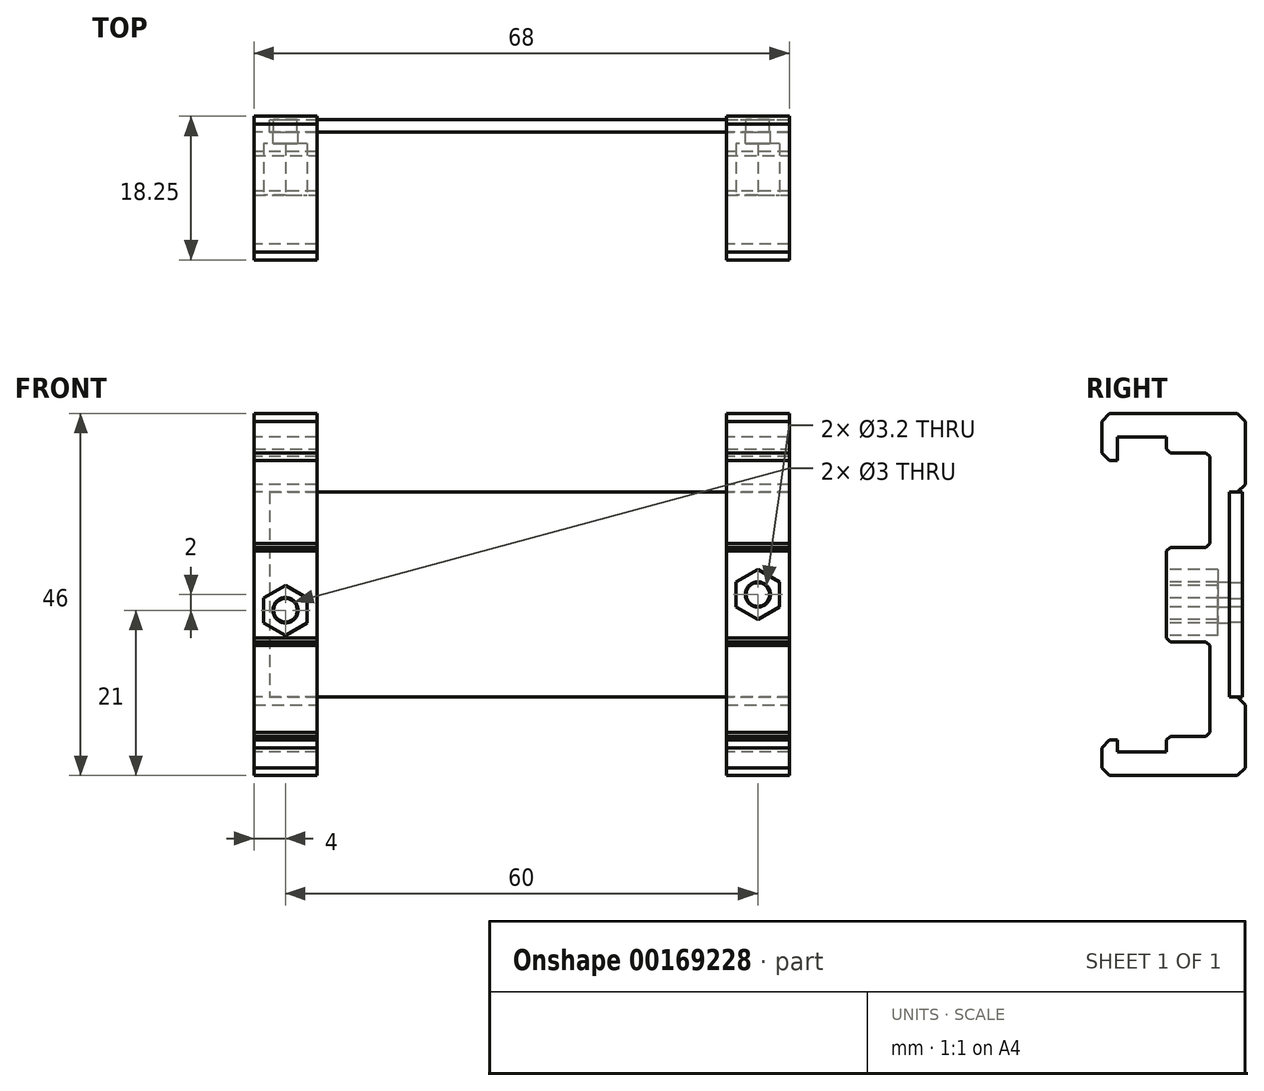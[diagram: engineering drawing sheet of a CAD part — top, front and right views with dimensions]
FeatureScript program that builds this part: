
annotation { "Feature Type Name" : "Feature", "Feature Type Description" : "" }
export const myFeature = defineFeature(function(context is Context, id is Id, definition is map)
    precondition{}
    {
        {
            var Q0;
            Q0=qCreatedBy(makeId("Front.planeOp"),FACE);
            var sketch = newSketch(context, id + "F0", { "sketchPlane" : qUnion([Q0])});
            skLineSegment(sketch, "E0.bottom", {"start": v(-33, 13) * mm, "end": v(33, 13) * mm});
            skLineSegment(sketch, "E0.top", {"start": v(-33, -13) * mm, "end": v(33, -13) * mm});
            skLineSegment(sketch, "E0.left", {"start": v(-33, 13) * mm, "end": v(-33, -13) * mm});
            skLineSegment(sketch, "E0.right", {"start": v(33, 13) * mm, "end": v(33, -13) * mm});
            skPoint(sketch, "E0.middle", {"position": v(0, 0) * mm});
            skCircle(sketch, "E1", {"center": v(-31, -2) * mm, "radius": 1.5 * mm});
            skCircle(sketch, "E2", {"center": v(29, 0) * mm, "radius": 1.5 * mm});
            skLineSegment(sketch, "E3", {"start": v(29, 0) * mm, "end": v(-31, 0) * mm, "construction": true});
            skSolve(sketch);
        }
        {
            var Q0;
            Q0=makeQuery(id+"F0.imprint","IMPRINT",FACE,{"disambiguationData":[TD([[makeQuery(id+"F0.imprint","IMPRINT",EDGE,{"derivedFrom":sQuery(id+"F0.wireOp",EDGE,"E0.bottom")}),-1.0]])]});
            extrude(context, id + "F1", {"entities" : qUnion([Q0]), "depth" : 1.6 * mm, "offsetDistance" : 25 * mm, "symmetric" : true});
        }
        {
            var Q0;
            Q0=sQuery(id+"F0.wireOp",VERTEX,"E2.center");
            var Q1;
            Q1=makeQuery(id+"F1.opExtrude","CAP_EDGE",EDGE,{"disambiguationData":[OSD([sQuery(id+"F0.wireOp",EDGE,"E0.bottom")])],"isStart":true});
            cPlane(context, id + "F2", {"entities" : qUnion([Q0, Q1]), "cplaneType" : CPlaneType.LINE_POINT, "offset" : 25 * mm, "width" : 150 * mm, "height" : 150 * mm});
        }
        {
            var Q0;
            Q0=qCreatedBy(id+"F2.planeOp",FACE);
            var sketch = newSketch(context, id + "F3", { "sketchPlane" : qUnion([Q0])});
            skLineSegment(sketch, "E4", {"start": v(-17.05, 17) * mm, "end": v(-17.05, 23) * mm});
            skLineSegment(sketch, "E5", {"start": v(-17.05, 23) * mm, "end": v(1.2, 23) * mm});
            skLineSegment(sketch, "E6", {"start": v(1.2, 23) * mm, "end": v(1.2, -23) * mm});
            skLineSegment(sketch, "E7", {"start": v(1.2, -23) * mm, "end": v(-17.05, -23) * mm});
            skLineSegment(sketch, "E8", {"start": v(-17.05, -23) * mm, "end": v(-17.05, -18.5) * mm});
            skLineSegment(sketch, "E9", {"start": v(-17.05, -18.5) * mm, "end": v(-15.05, -18.5) * mm});
            skLineSegment(sketch, "E10", {"start": v(-15.05, -18.5) * mm, "end": v(-15.05, -20) * mm});
            skLineSegment(sketch, "E11", {"start": v(-15.05, -20) * mm, "end": v(-8.8, -20) * mm});
            skLineSegment(sketch, "E12", {"start": v(-8.8, -20) * mm, "end": v(-8.8, 20) * mm});
            skLineSegment(sketch, "E13", {"start": v(-8.8, 20) * mm, "end": v(-15.05, 20) * mm});
            skLineSegment(sketch, "E14", {"start": v(-15.05, 20) * mm, "end": v(-15.05, 17) * mm});
            skLineSegment(sketch, "E15", {"start": v(-15.05, 17) * mm, "end": v(-17.05, 17) * mm});
            skPoint(sketch, "E16", {"position": v(1.2, 0) * mm});
            skLineSegment(sketch, "E17.0", {"start": v(-0.8, 13) * mm, "end": v(-0.8, -13) * mm});
            skLineSegment(sketch, "E18", {"start": v(-0.8, 13) * mm, "end": v(1.2, 13) * mm});
            skLineSegment(sketch, "E19", {"start": v(-0.8, -13) * mm, "end": v(1.2, -13) * mm});
            skLineSegment(sketch, "E20", {"start": v(-8.8, 18) * mm, "end": v(-3.3, 18) * mm});
            skLineSegment(sketch, "E21", {"start": v(-3.3, 18) * mm, "end": v(-3.3, 6) * mm});
            skLineSegment(sketch, "E22", {"start": v(-3.3, 6) * mm, "end": v(-8.8, 6) * mm});
            skLineSegment(sketch, "E23.MirrorCS", {"start": v(-8.8, -18) * mm, "end": v(-3.3, -18) * mm});
            skLineSegment(sketch, "E24.MirrorCS", {"start": v(-3.3, -18) * mm, "end": v(-3.3, -6) * mm});
            skLineSegment(sketch, "E25.MirrorCS", {"start": v(-3.3, -6) * mm, "end": v(-8.8, -6) * mm});
            skSolve(sketch);
        }
        {
            var Q0;
            Q0=makeQuery(id+"F3.imprint","IMPRINT",FACE,{"disambiguationData":[TD([[makeQuery(id+"F3.imprint","IMPRINT",EDGE,{"derivedFrom":sQuery(id+"F3.wireOp",EDGE,"E4")}),-1.0]])]});
            extrude(context, id + "F4", {"entities" : qUnion([Q0]), "depth" : 8 * mm, "offsetDistance" : 25 * mm, "symmetric" : true});
        }
        {
            var Q0;
            Q0=makeQuery(id+"F4.opExtrude","SWEPT_EDGE",EDGE,{"disambiguationData":[OSD([sQuery(id+"F3.wireOp",EDGE,"E12"),sQuery(id+"F3.wireOp",EDGE,"E20")])]});
            var Q1;
            Q1=makeQuery(id+"F4.opExtrude","SWEPT_EDGE",EDGE,{"disambiguationData":[OSD([sQuery(id+"F3.wireOp",EDGE,"E20"),sQuery(id+"F3.wireOp",EDGE,"E21")])]});
            var Q2;
            Q2=makeQuery(id+"F4.opExtrude","SWEPT_EDGE",EDGE,{"disambiguationData":[OSD([sQuery(id+"F3.wireOp",EDGE,"E21"),sQuery(id+"F3.wireOp",EDGE,"E22")])]});
            var Q3;
            Q3=makeQuery(id+"F4.opExtrude","SWEPT_EDGE",EDGE,{"disambiguationData":[OSD([sQuery(id+"F3.wireOp",EDGE,"E12"),sQuery(id+"F3.wireOp",EDGE,"E22")])]});
            var Q4;
            Q4=makeQuery(id+"F4.opExtrude","SWEPT_EDGE",EDGE,{"disambiguationData":[OSD([sQuery(id+"F3.wireOp",EDGE,"E12"),sQuery(id+"F3.wireOp",EDGE,"E25.MirrorCS")])]});
            var Q5;
            Q5=makeQuery(id+"F4.opExtrude","SWEPT_EDGE",EDGE,{"disambiguationData":[OSD([sQuery(id+"F3.wireOp",EDGE,"E24.MirrorCS"),sQuery(id+"F3.wireOp",EDGE,"E25.MirrorCS")])]});
            var Q6;
            Q6=makeQuery(id+"F4.opExtrude","SWEPT_EDGE",EDGE,{"disambiguationData":[OSD([sQuery(id+"F3.wireOp",EDGE,"E23.MirrorCS"),sQuery(id+"F3.wireOp",EDGE,"E24.MirrorCS")])]});
            var Q7;
            Q7=makeQuery(id+"F4.opExtrude","SWEPT_EDGE",EDGE,{"disambiguationData":[OSD([sQuery(id+"F3.wireOp",EDGE,"E12"),sQuery(id+"F3.wireOp",EDGE,"E23.MirrorCS")])]});
            chamfer(context, id + "F5", {"entities" : qUnion([Q0, Q1, Q2, Q3, Q4, Q5, Q6, Q7]), "width" : 0.5 * mm, "tangentPropagation" : true});
        }
        {
            var Q0;
            Q0=makeQuery(id+"F4.opExtrude","SWEPT_EDGE",EDGE,{"disambiguationData":[OSD([sQuery(id+"F3.wireOp",EDGE,"E6"),sQuery(id+"F3.wireOp",EDGE,"E7")])]});
            var Q1;
            Q1=makeQuery(id+"F4.opExtrude","SWEPT_EDGE",EDGE,{"disambiguationData":[OSD([sQuery(id+"F3.wireOp",EDGE,"E7"),sQuery(id+"F3.wireOp",EDGE,"E8")])]});
            var Q2;
            Q2=makeQuery(id+"F4.opExtrude","SWEPT_EDGE",EDGE,{"disambiguationData":[OSD([sQuery(id+"F3.wireOp",EDGE,"E4"),sQuery(id+"F3.wireOp",EDGE,"E5")])]});
            var Q3;
            Q3=makeQuery(id+"F4.opExtrude","SWEPT_EDGE",EDGE,{"disambiguationData":[OSD([sQuery(id+"F3.wireOp",EDGE,"E4"),sQuery(id+"F3.wireOp",EDGE,"E15")])]});
            var Q4;
            Q4=makeQuery(id+"F4.opExtrude","SWEPT_EDGE",EDGE,{"disambiguationData":[OSD([sQuery(id+"F3.wireOp",EDGE,"E8"),sQuery(id+"F3.wireOp",EDGE,"E9")])]});
            var Q5;
            Q5=makeQuery(id+"F4.opExtrude","SWEPT_EDGE",EDGE,{"disambiguationData":[OSD([sQuery(id+"F3.wireOp",EDGE,"E5"),sQuery(id+"F3.wireOp",EDGE,"E6")])]});
            var Q6;
            Q6=makeQuery(id+"F4.opExtrude","SWEPT_EDGE",EDGE,{"disambiguationData":[OSD([sQuery(id+"F3.wireOp",EDGE,"E6"),sQuery(id+"F3.wireOp",EDGE,"E18")])]});
            var Q7;
            Q7=makeQuery(id+"F4.opExtrude","SWEPT_EDGE",EDGE,{"disambiguationData":[OSD([sQuery(id+"F3.wireOp",EDGE,"E6"),sQuery(id+"F3.wireOp",EDGE,"E19")])]});
            chamfer(context, id + "F6", {"entities" : qUnion([Q0, Q1, Q2, Q3, Q4, Q5, Q6, Q7]), "width" : 1 * mm, "tangentPropagation" : true});
        }
        {
            var Q0;
            Q0=makeQuery(id+"FEOm17wwtYkwkif_3.splitOp","SPLIT",BODY,{"derivedFrom":makeQuery(id+"F4.opExtrude","SWEPT_BODY",BODY,{"disambiguationData":[OSD([sQuery(id+"F3.wireOp",EDGE,"E4"),sQuery(id+"F3.wireOp",EDGE,"E5"),sQuery(id+"F3.wireOp",EDGE,"E6"),sQuery(id+"F3.wireOp",EDGE,"E7"),sQuery(id+"F3.wireOp",EDGE,"E8"),sQuery(id+"F3.wireOp",EDGE,"E9"),sQuery(id+"F3.wireOp",EDGE,"E10"),sQuery(id+"F3.wireOp",EDGE,"E11"),sQuery(id+"F3.wireOp",EDGE,"E12"),sQuery(id+"F3.wireOp",EDGE,"E13"),sQuery(id+"F3.wireOp",EDGE,"E14"),sQuery(id+"F3.wireOp",EDGE,"E15")])]})});
            var Q1;
            Q1=makeQuery(id+"FEOm17wwtYkwkif_3.splitOp","SPLIT",BODY,{"derivedFrom":makeQuery(id+"F4.opExtrude","SWEPT_BODY",BODY,{"disambiguationData":[OSD([sQuery(id+"F3.wireOp",EDGE,"E4"),sQuery(id+"F3.wireOp",EDGE,"E5"),sQuery(id+"F3.wireOp",EDGE,"E6"),sQuery(id+"F3.wireOp",EDGE,"E7"),sQuery(id+"F3.wireOp",EDGE,"E8"),sQuery(id+"F3.wireOp",EDGE,"E9"),sQuery(id+"F3.wireOp",EDGE,"E10"),sQuery(id+"F3.wireOp",EDGE,"E11"),sQuery(id+"F3.wireOp",EDGE,"E12"),sQuery(id+"F3.wireOp",EDGE,"E13"),sQuery(id+"F3.wireOp",EDGE,"E14"),sQuery(id+"F3.wireOp",EDGE,"E15")])]}),"isFromBackBody":true});
            var Q2;
            Q2=sQuery(id+"F0.wireOp",EDGE,"E3");
            transform(context, id + "F7", {"entities" : qUnion([Q0, Q1]), "transformType" : TransformType.TRANSLATION_ENTITY, "oppositeDirectionEntity" : false, "transformLine" : qUnion([Q2]), "makeCopy" : true});
        }
        {
            var Q0;
            Q0=makeQuery(id+"F1.opExtrude","SWEPT_BODY",BODY,{"disambiguationData":[OSD([sQuery(id+"F0.wireOp",EDGE,"E0.bottom"),sQuery(id+"F0.wireOp",EDGE,"E0.top"),sQuery(id+"F0.wireOp",EDGE,"E0.left"),sQuery(id+"F0.wireOp",EDGE,"E0.right"),sQuery(id+"F0.wireOp",EDGE,"E1"),sQuery(id+"F0.wireOp",EDGE,"E2")])]});
            var Q1;
            Q1=makeQuery(id+"FEOm17wwtYkwkif_3.splitOp","SPLIT",BODY,{"derivedFrom":makeQuery(id+"F4.opExtrude","SWEPT_BODY",BODY,{"disambiguationData":[OSD([sQuery(id+"F3.wireOp",EDGE,"E4"),sQuery(id+"F3.wireOp",EDGE,"E5"),sQuery(id+"F3.wireOp",EDGE,"E6"),sQuery(id+"F3.wireOp",EDGE,"E7"),sQuery(id+"F3.wireOp",EDGE,"E8"),sQuery(id+"F3.wireOp",EDGE,"E9"),sQuery(id+"F3.wireOp",EDGE,"E10"),sQuery(id+"F3.wireOp",EDGE,"E11"),sQuery(id+"F3.wireOp",EDGE,"E12"),sQuery(id+"F3.wireOp",EDGE,"E13"),sQuery(id+"F3.wireOp",EDGE,"E14"),sQuery(id+"F3.wireOp",EDGE,"E15")])]}),"isFromBackBody":true});
            var Q2;
            Q2=makeQuery(id+"F7.opPattern","COPY",BODY,{"derivedFrom":makeQuery(id+"FEOm17wwtYkwkif_3.splitOp","SPLIT",BODY,{"derivedFrom":makeQuery(id+"F4.opExtrude","SWEPT_BODY",BODY,{"disambiguationData":[OSD([sQuery(id+"F3.wireOp",EDGE,"E4"),sQuery(id+"F3.wireOp",EDGE,"E5"),sQuery(id+"F3.wireOp",EDGE,"E6"),sQuery(id+"F3.wireOp",EDGE,"E7"),sQuery(id+"F3.wireOp",EDGE,"E8"),sQuery(id+"F3.wireOp",EDGE,"E9"),sQuery(id+"F3.wireOp",EDGE,"E10"),sQuery(id+"F3.wireOp",EDGE,"E11"),sQuery(id+"F3.wireOp",EDGE,"E12"),sQuery(id+"F3.wireOp",EDGE,"E13"),sQuery(id+"F3.wireOp",EDGE,"E14"),sQuery(id+"F3.wireOp",EDGE,"E15")])]}),"isFromBackBody":true}),"instanceName":"1"});
            booleanBodies(context, id + "F8", {"operationType" : BooleanOperationType.SUBTRACTION, "tools" : qUnion([Q0]), "targets" : qUnion([Q1, Q2]), "keepTools" : true});
        }
        {
            var Q0;
            Q0=makeQuery(id+"F7.opPattern","COPY",FACE,{"derivedFrom":makeQuery(id+"FEOm17wwtYkwkif_3.splitOp","SPLIT",FACE,{"derivedFrom":makeQuery(id+"F4.opExtrude","SWEPT_FACE",FACE,{"disambiguationData":[OSD([sQuery(id+"F3.wireOp",EDGE,"E12")])]}),"isFromBackBody":true}),"instanceName":"1"});
            var sketch = newSketch(context, id + "F9", { "sketchPlane" : qUnion([Q0])});
            skCircle(sketch, "E26.0", {"center": v(-31, -2) * mm, "radius": 1.5 * mm, "construction": true});
            skCircle(sketch, "E27.cCircle", {"center": v(-31, -2) * mm, "radius": 2.75 * mm, "construction": true});
            skLineSegment(sketch, "E27.0", {"start": v(-33.75, -3.59) * mm, "end": v(-33.75, -0.41) * mm});
            skLineSegment(sketch, "E27.1", {"start": v(-33.75, -0.41) * mm, "end": v(-31, 1.18) * mm});
            skLineSegment(sketch, "E27.2", {"start": v(-31, 1.18) * mm, "end": v(-28.25, -0.41) * mm});
            skLineSegment(sketch, "E27.3", {"start": v(-28.25, -0.41) * mm, "end": v(-28.25, -3.59) * mm});
            skLineSegment(sketch, "E27.4", {"start": v(-28.25, -3.59) * mm, "end": v(-31, -5.18) * mm});
            skLineSegment(sketch, "E27.5", {"start": v(-31, -5.18) * mm, "end": v(-33.75, -3.59) * mm});
            skPoint(sketch, "E27.0.midPoint", {"position": v(-33.75, -2) * mm});
            skCircle(sketch, "E28.0", {"center": v(29, 0) * mm, "radius": 1.5 * mm, "construction": true});
            skCircle(sketch, "E29.cCircle", {"center": v(29, 0) * mm, "radius": 2.75 * mm, "construction": true});
            skLineSegment(sketch, "E29.0", {"start": v(26.25, -1.59) * mm, "end": v(26.25, 1.59) * mm});
            skLineSegment(sketch, "E29.1", {"start": v(26.25, 1.59) * mm, "end": v(29, 3.18) * mm});
            skLineSegment(sketch, "E29.2", {"start": v(29, 3.18) * mm, "end": v(31.75, 1.59) * mm});
            skLineSegment(sketch, "E29.3", {"start": v(31.75, 1.59) * mm, "end": v(31.75, -1.59) * mm});
            skLineSegment(sketch, "E29.4", {"start": v(31.75, -1.59) * mm, "end": v(29, -3.18) * mm});
            skLineSegment(sketch, "E29.5", {"start": v(29, -3.18) * mm, "end": v(26.25, -1.59) * mm});
            skPoint(sketch, "E29.0.midPoint", {"position": v(26.25, 0) * mm});
            skSolve(sketch);
        }
        {
            var Q0;
            Q0=makeQuery(id+"F9.imprint","IMPRINT",FACE,{"disambiguationData":[TD([[makeQuery(id+"F9.imprint","IMPRINT",EDGE,{"derivedFrom":sQuery(id+"F9.wireOp",EDGE,"E27.0")}),-1.0]])]});
            var Q1;
            Q1=makeQuery(id+"F9.imprint","IMPRINT",FACE,{"disambiguationData":[TD([[makeQuery(id+"F9.imprint","IMPRINT",EDGE,{"derivedFrom":sQuery(id+"F9.wireOp",EDGE,"E29.0")}),-1.0]])]});
            extrude(context, id + "F10", {"entities" : qUnion([Q0, Q1]), "operationType" : NewBodyOperationType.REMOVE, "oppositeDirection" : true, "depth" : 6.5 * mm, "offsetDistance" : 25 * mm});
        }
        {
            var Q0;
            Q0=sQuery(id+"F9.wireOp",VERTEX,"E26.0.center");
            var Q1;
            Q1=sQuery(id+"F9.wireOp",VERTEX,"E28.0.center");
            var Q2;
            Q2=makeQuery(id+"FEOm17wwtYkwkif_3.splitOp","SPLIT",BODY,{"derivedFrom":makeQuery(id+"F4.opExtrude","SWEPT_BODY",BODY,{"disambiguationData":[OSD([sQuery(id+"F3.wireOp",EDGE,"E4"),sQuery(id+"F3.wireOp",EDGE,"E5"),sQuery(id+"F3.wireOp",EDGE,"E6"),sQuery(id+"F3.wireOp",EDGE,"E7"),sQuery(id+"F3.wireOp",EDGE,"E8"),sQuery(id+"F3.wireOp",EDGE,"E9"),sQuery(id+"F3.wireOp",EDGE,"E10"),sQuery(id+"F3.wireOp",EDGE,"E11"),sQuery(id+"F3.wireOp",EDGE,"E12"),sQuery(id+"F3.wireOp",EDGE,"E13"),sQuery(id+"F3.wireOp",EDGE,"E14"),sQuery(id+"F3.wireOp",EDGE,"E15")])]}),"isFromBackBody":true});
            var Q3;
            Q3=makeQuery(id+"F7.opPattern","COPY",BODY,{"derivedFrom":makeQuery(id+"FEOm17wwtYkwkif_3.splitOp","SPLIT",BODY,{"derivedFrom":makeQuery(id+"F4.opExtrude","SWEPT_BODY",BODY,{"disambiguationData":[OSD([sQuery(id+"F3.wireOp",EDGE,"E4"),sQuery(id+"F3.wireOp",EDGE,"E5"),sQuery(id+"F3.wireOp",EDGE,"E6"),sQuery(id+"F3.wireOp",EDGE,"E7"),sQuery(id+"F3.wireOp",EDGE,"E8"),sQuery(id+"F3.wireOp",EDGE,"E9"),sQuery(id+"F3.wireOp",EDGE,"E10"),sQuery(id+"F3.wireOp",EDGE,"E11"),sQuery(id+"F3.wireOp",EDGE,"E12"),sQuery(id+"F3.wireOp",EDGE,"E13"),sQuery(id+"F3.wireOp",EDGE,"E14"),sQuery(id+"F3.wireOp",EDGE,"E15")])]}),"isFromBackBody":true}),"instanceName":"1"});
            hole(context, id + "F11", {"style" : HoleStyle.SIMPLE, "endStyle" : HoleEndStyle.THROUGH, "holeDiameter" : 3.2 * mm, "majorDiameter" : 5 * mm, "tappedDepth" : 12 * mm, "tapClearance" : 3, "locations" : qUnion([Q0, Q1]), "scope" : qUnion([Q2, Q3])});
        }
    });
